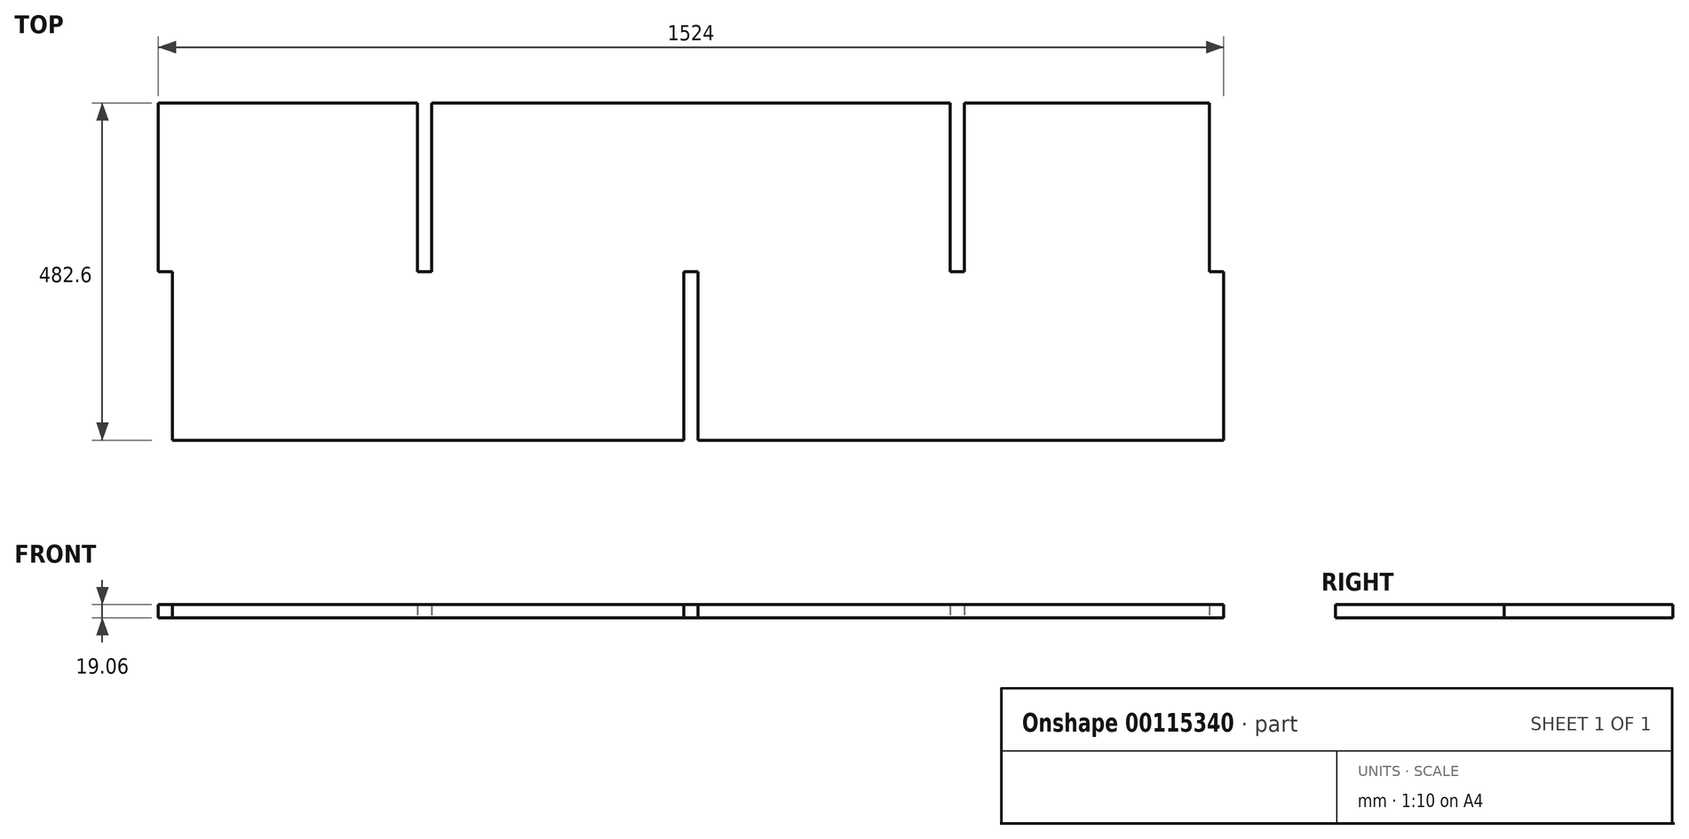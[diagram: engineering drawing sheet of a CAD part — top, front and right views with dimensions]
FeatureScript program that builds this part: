
annotation { "Feature Type Name" : "Feature", "Feature Type Description" : "" }
export const myFeature = defineFeature(function(context is Context, id is Id, definition is map)
    precondition{}
    {
        {
            var Q0;
            Q0=qCreatedBy(makeId("Top.planeOp"),FACE);
            var sketch = newSketch(context, id + "F0", { "sketchPlane" : qUnion([Q0])});
            skLineSegment(sketch, "E0", {"start": v(741.68, 241.3) * mm, "end": v(391.16, 241.3) * mm});
            skLineSegment(sketch, "E1", {"start": v(-762, 241.3) * mm, "end": v(-762, 0) * mm});
            skLineSegment(sketch, "E2", {"start": v(-741.68, -241.3) * mm, "end": v(-10.16, -241.3) * mm});
            skLineSegment(sketch, "E3", {"start": v(762, 0) * mm, "end": v(762, -241.3) * mm});
            skLineSegment(sketch, "E4", {"start": v(-762, 0) * mm, "end": v(-741.68, 0) * mm});
            skPoint(sketch, "E4.endSnap0", {"position": v(-762, 0) * mm});
            skLineSegment(sketch, "E5", {"start": v(-741.68, 0) * mm, "end": v(-741.68, -241.3) * mm});
            skLineSegment(sketch, "E6", {"start": v(762, 0) * mm, "end": v(741.68, 0) * mm});
            skLineSegment(sketch, "E7", {"start": v(741.68, 0) * mm, "end": v(741.68, 241.3) * mm});
            skLineSegment(sketch, "E8", {"start": v(-370.84, 0) * mm, "end": v(-370.84, 241.3) * mm});
            skLineSegment(sketch, "E9", {"start": v(-391.16, 0) * mm, "end": v(-391.16, 241.3) * mm});
            skLineSegment(sketch, "E10", {"start": v(-391.16, 0) * mm, "end": v(-370.84, 0) * mm});
            skLineSegment(sketch, "E11", {"start": v(10.16, 0) * mm, "end": v(10.16, -241.3) * mm});
            skLineSegment(sketch, "E12", {"start": v(-10.16, 0) * mm, "end": v(-10.16, -241.3) * mm});
            skLineSegment(sketch, "E13", {"start": v(-10.16, 0) * mm, "end": v(10.16, 0) * mm});
            skLineSegment(sketch, "E14.trimOffspring", {"start": v(-391.16, 241.3) * mm, "end": v(-762, 241.3) * mm});
            skPoint(sketch, "E15.orphan", {"position": v(-762, -241.3) * mm});
            skLineSegment(sketch, "E16.trimOffspring", {"start": v(10.16, -241.3) * mm, "end": v(762, -241.3) * mm});
            skPoint(sketch, "E17.orphan", {"position": v(762, 241.3) * mm});
            skLineSegment(sketch, "E18.trimOffspring", {"start": v(370.84, 241.3) * mm, "end": v(-370.84, 241.3) * mm});
            skLineSegment(sketch, "E19", {"start": v(370.84, 241.3) * mm, "end": v(370.84, 0) * mm});
            skLineSegment(sketch, "E20", {"start": v(391.16, 241.3) * mm, "end": v(391.16, 0) * mm});
            skLineSegment(sketch, "E21", {"start": v(370.84, 0) * mm, "end": v(391.16, 0) * mm});
            skSolve(sketch);
        }
        {
            var Q0;
            Q0=makeQuery(id+"F0.imprint","IMPRINT",FACE,{"disambiguationData":[TD([[makeQuery(id+"F0.imprint","IMPRINT",EDGE,{"derivedFrom":sQuery(id+"F0.wireOp",EDGE,"E0")}),1.0]])]});
            extrude(context, id + "F1", {"entities" : qUnion([Q0]), "endBound" : BoundingType.SYMMETRIC, "depth" : 19.05 * mm});
        }
    });
